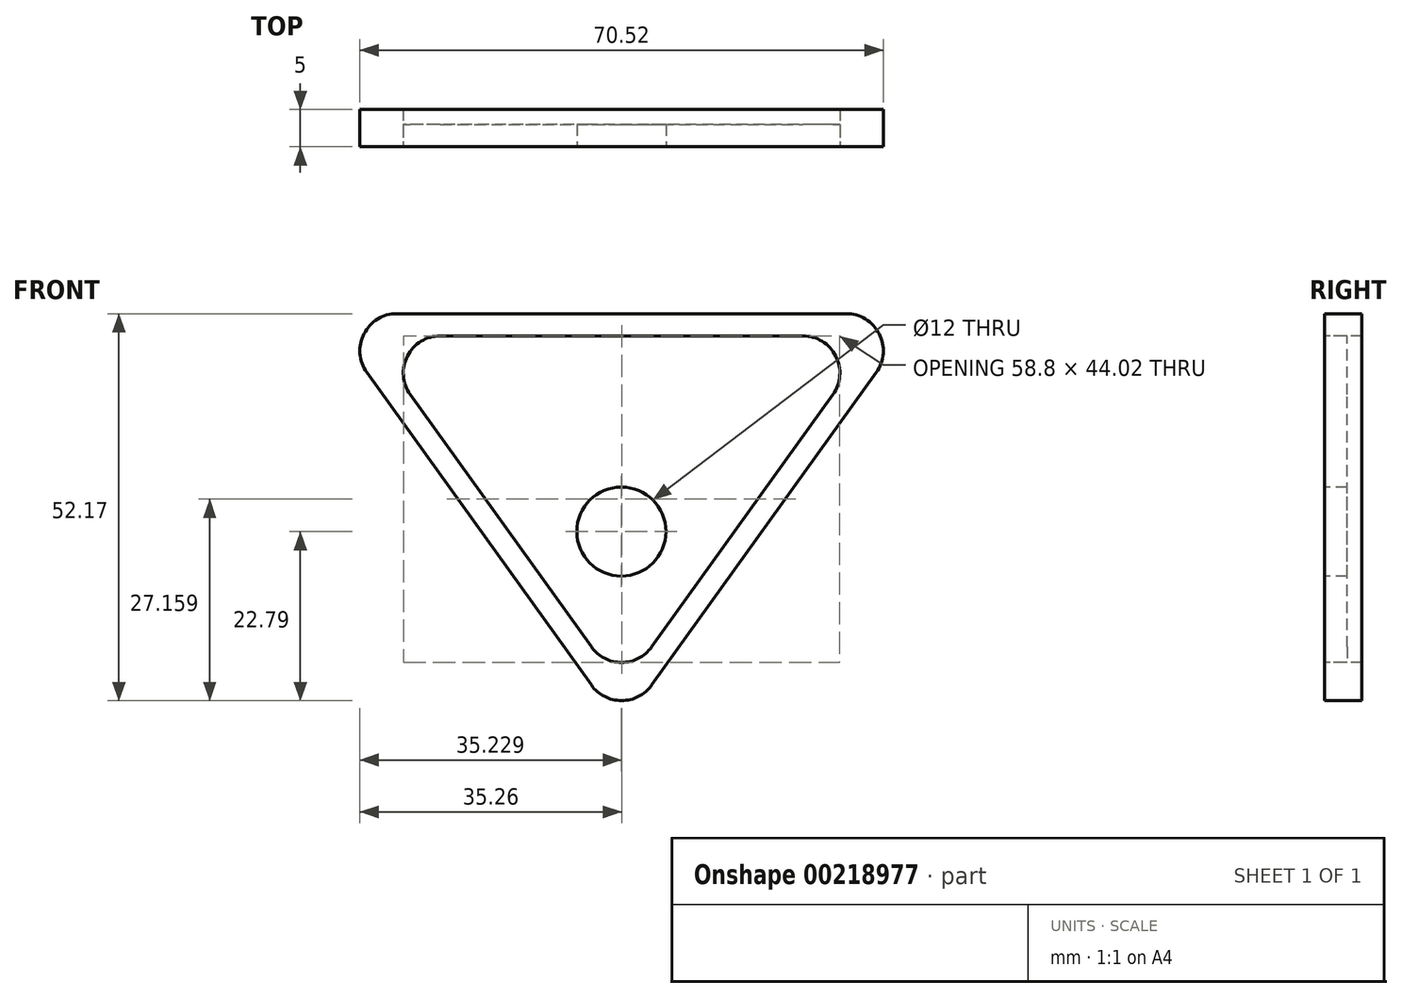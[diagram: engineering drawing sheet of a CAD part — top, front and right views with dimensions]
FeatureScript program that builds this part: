
annotation { "Feature Type Name" : "Feature", "Feature Type Description" : "" }
export const myFeature = defineFeature(function(context is Context, id is Id, definition is map)
    precondition{}
    {
        {
            var Q0;
            Q0=qCreatedBy(makeId("Front.planeOp"),FACE);
            var sketch = newSketch(context, id + "F0", { "sketchPlane" : qUnion([Q0])});
            skLineSegment(sketch, "E0", {"start": v(-9.74, 0) * mm, "end": v(-70.26, 0) * mm});
            skLineSegment(sketch, "E1", {"start": v(-74.32, -7.92) * mm, "end": v(-44.06, -50.08) * mm});
            skLineSegment(sketch, "E2", {"start": v(-35.94, -50.08) * mm, "end": v(-5.68, -7.92) * mm});
            skLineSegment(sketch, "E3", {"start": v(-11.52, -10.92) * mm, "end": v(-35.94, -44.94) * mm});
            skLineSegment(sketch, "E4", {"start": v(-44.06, -44.94) * mm, "end": v(-68.48, -10.92) * mm});
            skLineSegment(sketch, "E5", {"start": v(-64.41, -3) * mm, "end": v(-15.59, -3) * mm});
            skCircle(sketch, "E6", {"center": v(-40.03, -29.38) * mm, "radius": 6 * mm});
            skPoint(sketch, "E7.visualSharp", {"position": v(-40, -50.6) * mm});
            skArc(sketch, "E7.filletArc", {"start": v(-44.06, -44.94) * mm, "mid": v(-40, -47.02) * mm, "end": v(-35.94, -44.94) * mm});
            skPoint(sketch, "E8.visualSharp", {"position": v(-40, -55.74) * mm});
            skArc(sketch, "E8.filletArc", {"start": v(-44.06, -50.08) * mm, "mid": v(-40, -52.17) * mm, "end": v(-35.94, -50.08) * mm});
            skPoint(sketch, "E9.visualSharp", {"position": v(-74.15, -3) * mm});
            skArc(sketch, "E9.filletArc", {"start": v(-64.41, -3) * mm, "mid": v(-68.86, -5.72) * mm, "end": v(-68.48, -10.92) * mm});
            skPoint(sketch, "E10.visualSharp", {"position": v(-80, 0) * mm});
            skArc(sketch, "E10.filletArc", {"start": v(-70.26, 0) * mm, "mid": v(-74.7, -2.72) * mm, "end": v(-74.32, -7.92) * mm});
            skPoint(sketch, "E11.visualSharp", {"position": v(-5.85, -3) * mm});
            skArc(sketch, "E11.filletArc", {"start": v(-11.52, -10.92) * mm, "mid": v(-11.14, -5.72) * mm, "end": v(-15.59, -3) * mm});
            skPoint(sketch, "E12.visualSharp", {"position": v(0, 0) * mm});
            skArc(sketch, "E12.filletArc", {"start": v(-5.68, -7.92) * mm, "mid": v(-5.3, -2.72) * mm, "end": v(-9.74, 0) * mm});
            skSolve(sketch);
        }
        {
            var Q0;
            Q0=sQuery(id+"F0.wireOp",EDGE,"E6");
            extrude(context, id + "F1", {"bodyType" : ToolBodyType.SURFACE, "surfaceEntities" : qUnion([Q0]), "depth" : 50 * mm, "offsetDistance" : 25 * mm});
        }
        {
            var Q0;
            Q0=makeQuery(id+"F0.imprint","IMPRINT",FACE,{"disambiguationData":[TD([[makeQuery(id+"F0.imprint","IMPRINT",EDGE,{"derivedFrom":sQuery(id+"F0.wireOp",EDGE,"E0")}),1.0]])]});
            extrude(context, id + "F2", {"entities" : qUnion([Q0]), "oppositeDirection" : true, "depth" : 5 * mm, "offsetDistance" : 25 * mm});
        }
        {
            var Q0;
            Q0=makeQuery(id+"F0.imprint","IMPRINT",FACE,{"disambiguationData":[TD([[makeQuery(id+"F0.imprint","IMPRINT",EDGE,{"derivedFrom":sQuery(id+"F0.wireOp",EDGE,"E3")}),-1.0]])]});
            extrude(context, id + "F3", {"entities" : qUnion([Q0]), "oppositeDirection" : true, "depth" : 3 * mm, "offsetDistance" : 25 * mm});
        }
    });
